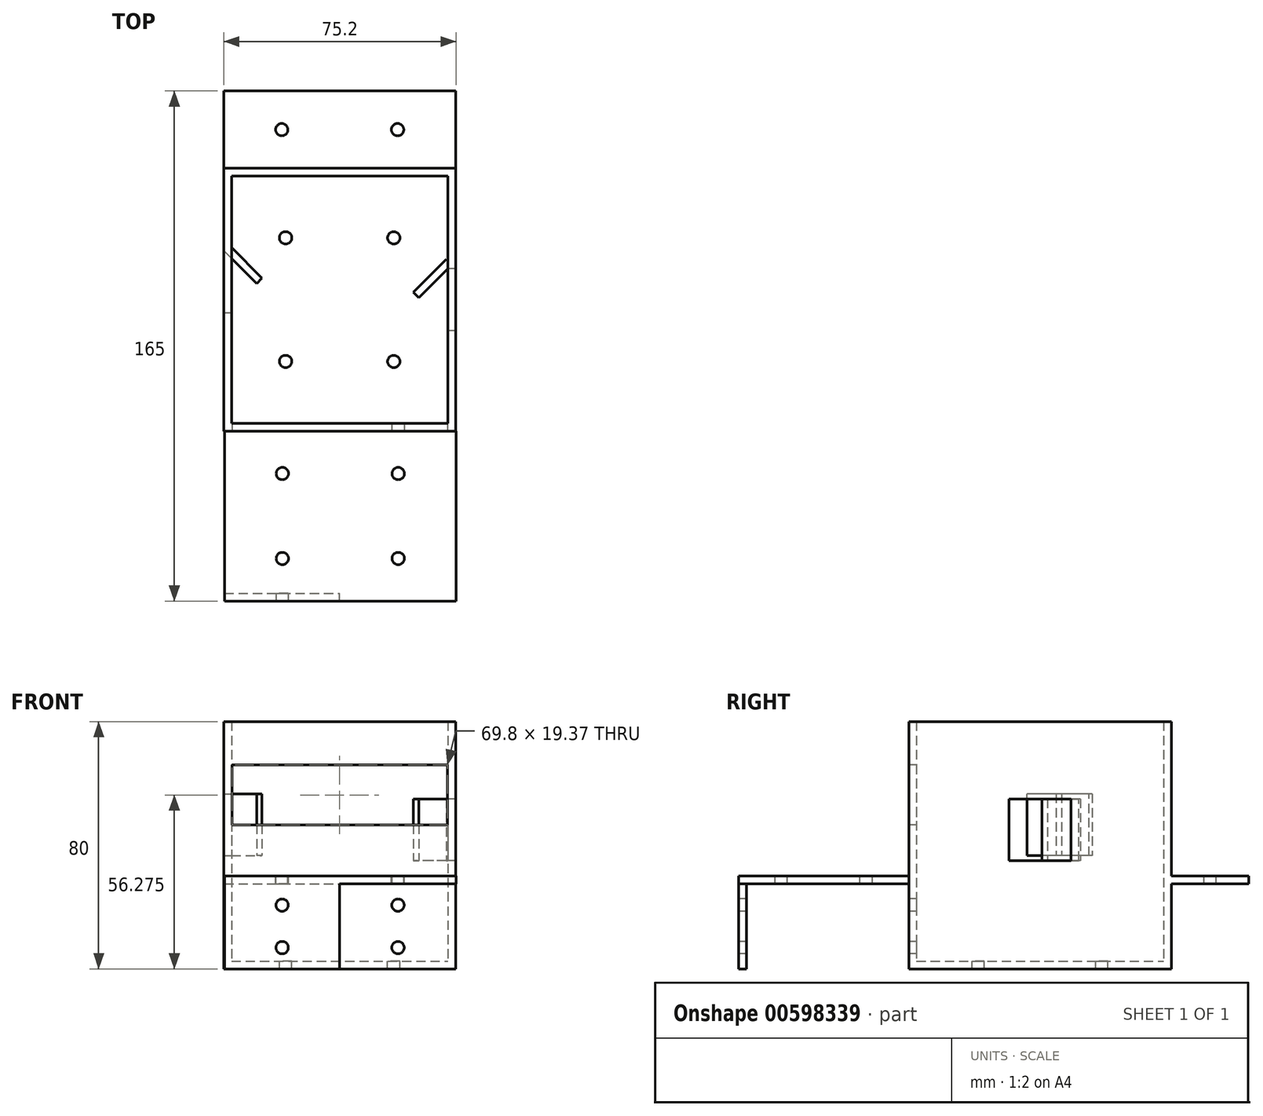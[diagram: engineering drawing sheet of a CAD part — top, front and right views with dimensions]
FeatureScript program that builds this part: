
annotation { "Feature Type Name" : "Feature", "Feature Type Description" : "" }
export const myFeature = defineFeature(function(context is Context, id is Id, definition is map)
    precondition{}
    {
        {
            var Q0;
            Q0=qCreatedBy(makeId("Top.planeOp"),FACE);
            var sketch = newSketch(context, id + "F0", { "sketchPlane" : qUnion([Q0])});
            skPoint(sketch, "E0", {"position": v(-37.5, -42.5) * mm});
            skPoint(sketch, "E1", {"position": v(37.5, 42.5) * mm});
            skLineSegment(sketch, "E2.bottom", {"start": v(-37.5, -42.5) * mm, "end": v(37.5, -42.5) * mm});
            skLineSegment(sketch, "E2.top", {"start": v(-37.5, 42.5) * mm, "end": v(37.5, 42.5) * mm});
            skLineSegment(sketch, "E2.left", {"start": v(-37.5, -42.5) * mm, "end": v(-37.5, 42.5) * mm});
            skLineSegment(sketch, "E2.right", {"start": v(37.5, -42.5) * mm, "end": v(37.5, 42.5) * mm});
            skSolve(sketch);
        }
        {
            var Q0;
            Q0=makeQuery(id+"F0.imprint","IMPRINT",FACE,{"disambiguationData":[TD([[makeQuery(id+"F0.imprint","IMPRINT",EDGE,{"derivedFrom":sQuery(id+"F0.wireOp",EDGE,"E2.bottom")}),1.0]])]});
            extrude(context, id + "F1", {"entities" : qUnion([Q0]), "depth" : 80 * mm, "offsetDistance" : 25.4 * mm});
        }
        {
            var Q0;
            Q0=makeQuery(id+"F1.opExtrude","CAP_FACE",FACE,{"disambiguationData":[OSD([sQuery(id+"F0.wireOp",EDGE,"E2.bottom"),sQuery(id+"F0.wireOp",EDGE,"E2.top"),sQuery(id+"F0.wireOp",EDGE,"E2.left"),sQuery(id+"F0.wireOp",EDGE,"E2.right")])],"isStart":false});
            shell(context, id + "F2", {"entities" : qUnion([Q0]), "thickness" : 2.5 * mm});
        }
        {
            var Q0;
            Q0=makeQuery(id+"F1.opExtrude","SWEPT_FACE",FACE,{"disambiguationData":[OSD([sQuery(id+"F0.wireOp",EDGE,"E2.bottom")])]});
            var sketch = newSketch(context, id + "F3", { "sketchPlane" : qUnion([Q0])});
            skPoint(sketch, "E3", {"position": v(-37.5, 65.96) * mm});
            skPoint(sketch, "E4", {"position": v(37.5, 66.59) * mm});
            skLineSegment(sketch, "E5", {"start": v(-37.5, 65.96) * mm, "end": v(-37.5, 45.96) * mm});
            skLineSegment(sketch, "E6", {"start": v(37.5, 66.59) * mm, "end": v(37.5, 46.59) * mm});
            skPoint(sketch, "E7", {"position": v(-37.5, 45.96) * mm});
            skLineSegment(sketch, "E8", {"start": v(-37.5, 65.96) * mm, "end": v(-34.9, 65.96) * mm});
            skLineSegment(sketch, "E9", {"start": v(37.5, 46.59) * mm, "end": v(34.9, 46.59) * mm});
            skLineSegment(sketch, "E10.bottom", {"start": v(-34.9, 65.96) * mm, "end": v(34.9, 65.96) * mm});
            skLineSegment(sketch, "E10.top", {"start": v(-34.9, 46.59) * mm, "end": v(34.9, 46.59) * mm});
            skLineSegment(sketch, "E10.left", {"start": v(-34.9, 65.96) * mm, "end": v(-34.9, 46.59) * mm});
            skLineSegment(sketch, "E10.right", {"start": v(34.9, 65.96) * mm, "end": v(34.9, 46.59) * mm});
            skSolve(sketch);
        }
        {
            var Q0;
            Q0=makeQuery(id+"F3.imprint","IMPRINT",FACE,{"disambiguationData":[TD([[makeQuery(id+"F3.imprint","IMPRINT",EDGE,{"derivedFrom":sQuery(id+"F3.wireOp",EDGE,"E10.bottom")}),-1.0]])]});
            extrude(context, id + "F4", {"entities" : qUnion([Q0]), "operationType" : NewBodyOperationType.REMOVE, "oppositeDirection" : true, "depth" : 2.5 * mm, "offsetDistance" : 25.4 * mm});
        }
        {
            var Q0;
            Q0=qCreatedBy(makeId("Right.planeOp"),FACE);
            var sketch = newSketch(context, id + "F5", { "sketchPlane" : qUnion([Q0])});
            skPoint(sketch, "E11", {"position": v(5.82, 46.62) * mm});
            skLineSegment(sketch, "E12.bottom", {"start": v(-4.18, 56.62) * mm, "end": v(15.82, 56.62) * mm});
            skLineSegment(sketch, "E12.top", {"start": v(-4.18, 36.62) * mm, "end": v(15.82, 36.62) * mm});
            skLineSegment(sketch, "E12.left", {"start": v(-4.18, 56.62) * mm, "end": v(-4.18, 36.62) * mm});
            skLineSegment(sketch, "E12.right", {"start": v(15.82, 56.62) * mm, "end": v(15.82, 36.62) * mm});
            skSolve(sketch);
        }
        {
            var Q0;
            Q0 = qSketchRegion(id + "F5", true);
            extrude(context, id + "F6", {"entities" : qUnion([Q0]), "operationType" : NewBodyOperationType.REMOVE, "oppositeDirection" : true, "depth" : 85 * mm, "offsetDistance" : 25.4 * mm});
        }
        {
            var Q0;
            Q0=qCreatedBy(makeId("Right.planeOp"),FACE);
            var sketch = newSketch(context, id + "F7", { "sketchPlane" : qUnion([Q0])});
            skLineSegment(sketch, "E13.bottom", {"start": v(10, 55) * mm, "end": v(-10, 55) * mm});
            skLineSegment(sketch, "E13.top", {"start": v(10, 35) * mm, "end": v(-10, 35) * mm});
            skLineSegment(sketch, "E13.left", {"start": v(10, 55) * mm, "end": v(10, 35) * mm});
            skLineSegment(sketch, "E13.right", {"start": v(-10, 55) * mm, "end": v(-10, 35) * mm});
            skPoint(sketch, "E13.middle", {"position": v(0, 45) * mm});
            skSolve(sketch);
        }
        {
            var Q0;
            Q0 = qSketchRegion(id + "F7", true);
            extrude(context, id + "F8", {"entities" : qUnion([Q0]), "operationType" : NewBodyOperationType.REMOVE, "depth" : 40 * mm, "offsetDistance" : 25.4 * mm});
        }
        {
            var Q0;
            Q0=makeQuery(id+"F8.boolean.opBoolean","INTERSECT",EDGE,{"derivedFrom":[makeQuery(id+"F2.opShell","OFFSET_FACE",FACE,{"disambiguationData":[OSD([sQuery(id+"F0.wireOp",EDGE,"E2.right")])]}),makeQuery(id+"F8.opExtrude","SWEPT_FACE",FACE,{"disambiguationData":[OSD([sQuery(id+"F7.wireOp",EDGE,"E13.left")])]})]});
            cPlane(context, id + "F9", {"entities" : qUnion([Q0]), "cplaneType" : CPlaneType.LINE_ANGLE, "offset" : 25.4 * mm, "angle" : 45 * degree, "width" : 152.4 * mm, "height" : 152.4 * mm});
        }
        {
            var Q0;
            Q0=makeQuery(id+"F1.opExtrude","SWEPT_FACE",FACE,{"disambiguationData":[OSD([sQuery(id+"F0.wireOp",EDGE,"E2.bottom")])]});
            var sketch = newSketch(context, id + "F10", { "sketchPlane" : qUnion([Q0])});
            skLineSegment(sketch, "E14", {"start": v(0, 0) * mm, "end": v(0, 27.5) * mm});
            skPoint(sketch, "E14.endSnap0", {"position": v(0, 0) * mm});
            skLineSegment(sketch, "E15", {"start": v(0, 27.5) * mm, "end": v(37.5, 27.5) * mm});
            skLineSegment(sketch, "E16", {"start": v(37.5, 27.5) * mm, "end": v(-37.5, 27.5) * mm});
            skSolve(sketch);
        }
        {
            var Q0;
            Q0=sQuery(id+"F10.wireOp",EDGE,"E16");
            cPlane(context, id + "F11", {"entities" : qUnion([Q0]), "cplaneType" : CPlaneType.LINE_ANGLE, "offset" : 25.4 * mm, "angle" : 90 * degree, "width" : 152.4 * mm, "height" : 152.4 * mm});
        }
        {
            var Q0;
            Q0=qCreatedBy(id+"F11.planeOp",FACE);
            var sketch = newSketch(context, id + "F12", { "sketchPlane" : qUnion([Q0])});
            skLineSegment(sketch, "E17", {"start": v(0.2, 0) * mm, "end": v(0.2, -42.5) * mm});
            skLineSegment(sketch, "E18", {"start": v(0.2, -42.5) * mm, "end": v(37.7, -42.5) * mm});
            skLineSegment(sketch, "E19", {"start": v(37.7, -42.5) * mm, "end": v(37.7, -95) * mm});
            skLineSegment(sketch, "E20", {"start": v(0.2, -42.5) * mm, "end": v(-37.3, -42.5) * mm});
            skLineSegment(sketch, "E21.bottom", {"start": v(-37.3, -42.5) * mm, "end": v(37.7, -42.5) * mm});
            skLineSegment(sketch, "E21.top", {"start": v(-37.3, -95) * mm, "end": v(37.7, -95) * mm});
            skLineSegment(sketch, "E21.left", {"start": v(-37.3, -42.5) * mm, "end": v(-37.3, -95) * mm});
            skSolve(sketch);
        }
        {
            var Q0;
            Q0=makeQuery(id+"F12.imprint","IMPRINT",FACE,{"disambiguationData":[TD([[makeQuery(id+"F12.imprint","IMPRINT",EDGE,{"derivedFrom":sQuery(id+"F12.wireOp",EDGE,"E21.top")}),1.0]])]});
            extrude(context, id + "F13", {"entities" : qUnion([Q0]), "operationType" : NewBodyOperationType.ADD, "depth" : 2.5 * mm, "offsetDistance" : 25.4 * mm});
        }
        {
            var Q0;
            Q0=makeQuery(id+"F13.opExtrude","SWEPT_FACE",FACE,{"disambiguationData":[OSD([sQuery(id+"F12.wireOp",EDGE,"E21.top")])]});
            var sketch = newSketch(context, id + "F14", { "sketchPlane" : qUnion([Q0])});
            skLineSegment(sketch, "E22", {"start": v(0.2, 27.5) * mm, "end": v(0, -7.5) * mm});
            skLineSegment(sketch, "E23.bottom", {"start": v(0, 0) * mm, "end": v(37.7, 0) * mm});
            skLineSegment(sketch, "E23.top", {"start": v(0, 27.5) * mm, "end": v(37.7, 27.5) * mm});
            skLineSegment(sketch, "E23.left", {"start": v(0, 0) * mm, "end": v(0, 27.5) * mm});
            skLineSegment(sketch, "E23.right", {"start": v(37.7, 0) * mm, "end": v(37.7, 27.5) * mm});
            skLineSegment(sketch, "E24.bottom", {"start": v(0, 0) * mm, "end": v(-37.3, 0) * mm});
            skLineSegment(sketch, "E24.top", {"start": v(0, 27.5) * mm, "end": v(-37.3, 27.5) * mm});
            skLineSegment(sketch, "E24.right", {"start": v(-37.3, 0) * mm, "end": v(-37.3, 27.5) * mm});
            skPoint(sketch, "E25", {"position": v(37.7, 0) * mm});
            skPoint(sketch, "E26", {"position": v(-37.3, 27.5) * mm});
            skLineSegment(sketch, "E27.bottom", {"start": v(-37.3, 27.5) * mm, "end": v(37.7, 27.5) * mm});
            skLineSegment(sketch, "E27.top", {"start": v(-37.3, 0) * mm, "end": v(37.7, 0) * mm});
            skLineSegment(sketch, "E27.left", {"start": v(-37.3, 27.5) * mm, "end": v(-37.3, 0) * mm});
            skLineSegment(sketch, "E27.right", {"start": v(37.7, 27.5) * mm, "end": v(37.7, 0) * mm});
            skSolve(sketch);
        }
        {
            var Q0;
            Q0=qCreatedBy(id+"F9.planeOp",FACE);
            var sketch = newSketch(context, id + "F15", { "sketchPlane" : qUnion([Q0])});
            skLineSegment(sketch, "E28.0", {"start": v(-33.59, 55) * mm, "end": v(-33.59, 35) * mm});
            skLineSegment(sketch, "E29.bottom", {"start": v(-33.59, 55) * mm, "end": v(-18.59, 55) * mm});
            skLineSegment(sketch, "E29.top", {"start": v(-33.59, 35) * mm, "end": v(-18.59, 35) * mm});
            skLineSegment(sketch, "E29.right", {"start": v(-18.59, 55) * mm, "end": v(-18.59, 35) * mm});
            skPoint(sketch, "E30.0", {"position": v(28.28, 2.5) * mm});
            skSolve(sketch);
        }
        {
            var Q0;
            Q0=makeQuery(id+"F15.imprint","IMPRINT",FACE,{"disambiguationData":[TD([[makeQuery(id+"F15.imprint","IMPRINT",EDGE,{"derivedFrom":sQuery(id+"F15.wireOp",EDGE,"E29.bottom")}),-1.0]])]});
            extrude(context, id + "F16", {"entities" : qUnion([Q0]), "operationType" : NewBodyOperationType.ADD, "depth" : 2.5 * mm, "offsetDistance" : 25 * mm});
        }
        {
            var Q0;
            Q0=makeQuery(id+"F6.boolean.opBoolean","INTERSECT",EDGE,{"derivedFrom":[makeQuery(id+"F1.opExtrude","SWEPT_FACE",FACE,{"disambiguationData":[OSD([sQuery(id+"F0.wireOp",EDGE,"E2.left")])]}),makeQuery(id+"F6.opExtrude","SWEPT_FACE",FACE,{"disambiguationData":[OSD([sQuery(id+"F5.wireOp",EDGE,"E12.right")])]})]});
            cPlane(context, id + "F17", {"entities" : qUnion([Q0]), "cplaneType" : CPlaneType.LINE_ANGLE, "offset" : 25 * mm, "angle" : 45 * degree, "width" : 150 * mm, "height" : 150 * mm});
        }
        {
            var Q0;
            Q0=qCreatedBy(id+"F17.planeOp",FACE);
            var sketch = newSketch(context, id + "F18", { "sketchPlane" : qUnion([Q0])});
            skLineSegment(sketch, "E31.0", {"start": v(37.7, 36.62) * mm, "end": v(37.7, 56.62) * mm});
            skLineSegment(sketch, "E32.bottom", {"start": v(37.7, 56.62) * mm, "end": v(37.7, 56.62) * mm});
            skLineSegment(sketch, "E32.top", {"start": v(37.7, 36.62) * mm, "end": v(37.7, 36.62) * mm});
            skLineSegment(sketch, "E32.left", {"start": v(37.7, 56.62) * mm, "end": v(37.7, 36.62) * mm});
            skLineSegment(sketch, "E32.right", {"start": v(37.7, 56.62) * mm, "end": v(37.7, 36.62) * mm});
            skLineSegment(sketch, "E33.bottom", {"start": v(37.7, 56.62) * mm, "end": v(22.7, 56.62) * mm});
            skLineSegment(sketch, "E33.top", {"start": v(37.7, 36.62) * mm, "end": v(22.7, 36.62) * mm});
            skLineSegment(sketch, "E33.right", {"start": v(22.7, 56.62) * mm, "end": v(22.7, 36.62) * mm});
            skSolve(sketch);
        }
        {
            var Q0;
            Q0=makeQuery(id+"F18.imprint","IMPRINT",FACE,{"disambiguationData":[TD([[makeQuery(id+"F18.imprint","IMPRINT",EDGE,{"derivedFrom":sQuery(id+"F18.wireOp",EDGE,"E33.bottom")}),1.0]])]});
            extrude(context, id + "F19", {"entities" : qUnion([Q0]), "operationType" : NewBodyOperationType.ADD, "depth" : 2.5 * mm, "offsetDistance" : 25 * mm});
        }
        {
            var Q0;
            {var subQ0=sQuery(id+"F14.wireOp",EDGE,"E23.left");Q0=makeQuery(id+"F14.imprint","IMPRINT",FACE,{"disambiguationData":[TD([[makeQuery(id+"F14.imprint","IMPRINT",EDGE,{"derivedFrom":subQ0}),1.0]])]});}
            var Q1;
            {var subQ5=sQuery(id+"F14.wireOp",EDGE,"E27.right");Q1=makeQuery(id+"F14.imprint","IMPRINT",FACE,{"disambiguationData":[TD([[makeQuery(id+"F14.imprint","IMPRINT",EDGE,{"derivedFrom":subQ5}),-1.0]])]});}
            var Q2;
            {var subQ0=sQuery(id+"F12.wireOp",EDGE,"E21.top");Q2=makeQuery(id+"F14.imprint","IMPRINT",FACE,{"disambiguationData":[TD([[makeQuery(id+"F14.imprint","IMPRINT",EDGE,{"derivedFrom":makeQuery(id+"F13.opExtrude","CAP_EDGE",EDGE,{"disambiguationData":[OSD([subQ0])],"isStart":false})}),-1.0]])]});}
            extrude(context, id + "F20", {"entities" : qUnion([Q0, Q1, Q2]), "operationType" : NewBodyOperationType.ADD, "depth" : 2.5 * mm, "offsetDistance" : 25 * mm});
        }
        {
            var Q0;
            Q0=qCreatedBy(id+"F11.planeOp",FACE);
            var sketch = newSketch(context, id + "F21", { "sketchPlane" : qUnion([Q0])});
            skLineSegment(sketch, "E34", {"start": v(0, 0) * mm, "end": v(0, 42.5) * mm});
            skPoint(sketch, "E35", {"position": v(0, 42.5) * mm});
            skLineSegment(sketch, "E36", {"start": v(0, 42.5) * mm, "end": v(-37.5, 42.5) * mm});
            skLineSegment(sketch, "E37", {"start": v(-37.5, 42.5) * mm, "end": v(-37.5, 67.5) * mm});
            skLineSegment(sketch, "E38", {"start": v(0, 42.5) * mm, "end": v(37.5, 42.5) * mm});
            skLineSegment(sketch, "E39.bottom", {"start": v(37.5, 42.5) * mm, "end": v(-37.5, 42.5) * mm});
            skLineSegment(sketch, "E39.top", {"start": v(37.5, 67.5) * mm, "end": v(-37.5, 67.5) * mm});
            skLineSegment(sketch, "E39.left", {"start": v(37.5, 42.5) * mm, "end": v(37.5, 67.5) * mm});
            skLineSegment(sketch, "E40", {"start": v(0, 42.5) * mm, "end": v(0, 55) * mm});
            skLineSegment(sketch, "E41", {"start": v(0, 55) * mm, "end": v(18.75, 55) * mm});
            skLineSegment(sketch, "E42", {"start": v(0, 55) * mm, "end": v(-18.75, 55) * mm});
            skPoint(sketch, "E43", {"position": v(-18.75, 55) * mm});
            skPoint(sketch, "E44", {"position": v(18.75, 55) * mm});
            skSolve(sketch);
        }
        {
            var Q0;
            Q0=makeQuery(id+"F21.imprint","IMPRINT",FACE,{"disambiguationData":[TD([[makeQuery(id+"F21.imprint","IMPRINT",EDGE,{"derivedFrom":sQuery(id+"F21.wireOp",EDGE,"E39.top")}),1.0]])]});
            extrude(context, id + "F22", {"entities" : qUnion([Q0]), "operationType" : NewBodyOperationType.ADD, "depth" : 2.5 * mm, "offsetDistance" : 25 * mm});
        }
        {
            var Q0;
            Q0=makeQuery(id+"F22.opExtrude","CAP_FACE",FACE,{"disambiguationData":[OSD([sQuery(id+"F21.wireOp",EDGE,"E39.bottom"),sQuery(id+"F21.wireOp",EDGE,"E39.top"),sQuery(id+"F21.wireOp",EDGE,"E39.left"),sQuery(id+"F21.wireOp",EDGE,"E37")])],"isStart":false});
            var sketch = newSketch(context, id + "F23", { "sketchPlane" : qUnion([Q0])});
            skPoint(sketch, "E45.endSnap0", {"position": v(0, 42.5) * mm});
            skPoint(sketch, "E46", {"position": v(-18.75, 55) * mm});
            skPoint(sketch, "E47", {"position": v(18.75, 55) * mm});
            skCircle(sketch, "E48", {"center": v(-18.75, 55) * mm, "radius": 2 * mm});
            skCircle(sketch, "E49", {"center": v(18.75, 55) * mm, "radius": 2 * mm});
            skSolve(sketch);
        }
        {
            var Q0;
            Q0=sQuery(id+"F23.wireOp",VERTEX,"E46");
            var Q1;
            Q1=sQuery(id+"F23.wireOp",VERTEX,"E47");
            var Q2;
            Q2=makeQuery(id+"F1.opExtrude","SWEPT_BODY",BODY,{"disambiguationData":[OSD([sQuery(id+"F0.wireOp",EDGE,"E2.bottom"),sQuery(id+"F0.wireOp",EDGE,"E2.top"),sQuery(id+"F0.wireOp",EDGE,"E2.left"),sQuery(id+"F0.wireOp",EDGE,"E2.right")])]});
            hole(context, id + "F24", {"style" : HoleStyle.SIMPLE, "endStyle" : HoleEndStyle.THROUGH, "holeDiameter" : 4 * mm, "majorDiameter" : 5 * mm, "isTappedThrough" : true, "tappedDepth" : 12 * mm, "tapClearance" : 3, "locations" : qUnion([Q0, Q1]), "scope" : qUnion([Q2])});
        }
        {
            var Q0;
            Q0=makeQuery(id+"F20.opExtrude","CAP_FACE",FACE,{"disambiguationData":[OSD([sQuery(id+"F12.wireOp",EDGE,"E21.top"),sQuery(id+"F12.wireOp",EDGE,"E21.left"),sQuery(id+"F12.wireOp",EDGE,"E19"),sQuery(id+"F14.wireOp",EDGE,"E22"),sQuery(id+"F14.wireOp",EDGE,"E23.left"),sQuery(id+"F14.wireOp",EDGE,"E27.bottom"),sQuery(id+"F14.wireOp",EDGE,"E27.top"),sQuery(id+"F14.wireOp",EDGE,"E27.left"),sQuery(id+"F14.wireOp",EDGE,"E27.right")])],"isStart":false});
            var sketch = newSketch(context, id + "F25", { "sketchPlane" : qUnion([Q0])});
            skPoint(sketch, "E50", {"position": v(-18.63, 20.62) * mm});
            skPoint(sketch, "E51", {"position": v(-18.63, 6.87) * mm});
            skPoint(sketch, "E52", {"position": v(18.87, 6.87) * mm});
            skPoint(sketch, "E53", {"position": v(18.87, 20.62) * mm});
            skSolve(sketch);
        }
        {
            var Q0;
            Q0=sQuery(id+"F25.wireOp",VERTEX,"E50");
            var Q1;
            Q1=sQuery(id+"F25.wireOp",VERTEX,"E51");
            var Q2;
            Q2=sQuery(id+"F25.wireOp",VERTEX,"E52");
            var Q3;
            Q3=sQuery(id+"F25.wireOp",VERTEX,"E53");
            var Q4;
            Q4=makeQuery(id+"F1.opExtrude","SWEPT_BODY",BODY,{"disambiguationData":[OSD([sQuery(id+"F0.wireOp",EDGE,"E2.bottom"),sQuery(id+"F0.wireOp",EDGE,"E2.top"),sQuery(id+"F0.wireOp",EDGE,"E2.left"),sQuery(id+"F0.wireOp",EDGE,"E2.right")])]});
            hole(context, id + "F26", {"style" : HoleStyle.SIMPLE, "endStyle" : HoleEndStyle.BLIND, "holeDiameter" : 4 * mm, "majorDiameter" : 5 * mm, "holeDepth" : 12 * mm, "isTappedThrough" : true, "tappedDepth" : 12 * mm, "tapClearance" : 3, "locations" : qUnion([Q0, Q1, Q2, Q3]), "scope" : qUnion([Q4])});
        }
        {
            var Q0;
            {var subQ0=sQuery(id+"F12.wireOp",EDGE,"E21.top");Q0=makeQuery(id+"F20.boolean.opBoolean","MERGE",FACE,{"derivedFrom":[makeQuery(id+"F13.opExtrude","CAP_FACE",FACE,{"disambiguationData":[OSD([sQuery(id+"F12.wireOp",EDGE,"E21.bottom"),subQ0,sQuery(id+"F12.wireOp",EDGE,"E21.left"),sQuery(id+"F12.wireOp",EDGE,"E19")])],"isStart":false}),makeQuery(id+"F20.opExtrude","SWEPT_FACE",FACE,{"disambiguationData":[OSD([subQ0])]})]});}
            var sketch = newSketch(context, id + "F27", { "sketchPlane" : qUnion([Q0])});
            skPoint(sketch, "E54", {"position": v(-18.55, -56.25) * mm});
            skPoint(sketch, "E55", {"position": v(18.95, -56.25) * mm});
            skPoint(sketch, "E56", {"position": v(18.95, -83.75) * mm});
            skPoint(sketch, "E57", {"position": v(-18.55, -83.75) * mm});
            skSolve(sketch);
        }
        {
            var Q0;
            Q0=sQuery(id+"F27.wireOp",VERTEX,"E54");
            var Q1;
            Q1=sQuery(id+"F27.wireOp",VERTEX,"E55");
            var Q2;
            Q2=sQuery(id+"F27.wireOp",VERTEX,"E56");
            var Q3;
            Q3=sQuery(id+"F27.wireOp",VERTEX,"E57");
            var Q4;
            Q4=makeQuery(id+"F1.opExtrude","SWEPT_BODY",BODY,{"disambiguationData":[OSD([sQuery(id+"F0.wireOp",EDGE,"E2.bottom"),sQuery(id+"F0.wireOp",EDGE,"E2.top"),sQuery(id+"F0.wireOp",EDGE,"E2.left"),sQuery(id+"F0.wireOp",EDGE,"E2.right")])]});
            hole(context, id + "F28", {"style" : HoleStyle.SIMPLE, "endStyle" : HoleEndStyle.BLIND, "holeDiameter" : 4 * mm, "majorDiameter" : 5 * mm, "holeDepth" : 12 * mm, "isTappedThrough" : true, "tappedDepth" : 12 * mm, "tapClearance" : 3, "locations" : qUnion([Q0, Q1, Q2, Q3]), "scope" : qUnion([Q4])});
        }
        {
            var Q0;
            Q0=makeQuery(id+"F2.opShell","OFFSET_FACE",FACE,{"disambiguationData":[OSD([sQuery(id+"F0.wireOp",EDGE,"E2.bottom"),sQuery(id+"F0.wireOp",EDGE,"E2.top"),sQuery(id+"F0.wireOp",EDGE,"E2.left"),sQuery(id+"F0.wireOp",EDGE,"E2.right")])]});
            var sketch = newSketch(context, id + "F29", { "sketchPlane" : qUnion([Q0])});
            skPoint(sketch, "E58", {"position": v(-17.5, 20) * mm});
            skPoint(sketch, "E59", {"position": v(17.5, 20) * mm});
            skPoint(sketch, "E60", {"position": v(-17.5, -20) * mm});
            skPoint(sketch, "E61", {"position": v(17.5, -20) * mm});
            skSolve(sketch);
        }
        {
            var Q0;
            Q0=sQuery(id+"F29.wireOp",VERTEX,"E58");
            var Q1;
            Q1=sQuery(id+"F29.wireOp",VERTEX,"E59");
            var Q2;
            Q2=sQuery(id+"F29.wireOp",VERTEX,"E60");
            var Q3;
            Q3=sQuery(id+"F29.wireOp",VERTEX,"E61");
            var Q4;
            Q4=makeQuery(id+"F1.opExtrude","SWEPT_BODY",BODY,{"disambiguationData":[OSD([sQuery(id+"F0.wireOp",EDGE,"E2.bottom"),sQuery(id+"F0.wireOp",EDGE,"E2.top"),sQuery(id+"F0.wireOp",EDGE,"E2.left"),sQuery(id+"F0.wireOp",EDGE,"E2.right")])]});
            hole(context, id + "F30", {"style" : HoleStyle.SIMPLE, "endStyle" : HoleEndStyle.BLIND, "holeDiameter" : 4 * mm, "majorDiameter" : 5 * mm, "holeDepth" : 12 * mm, "isTappedThrough" : true, "tappedDepth" : 12 * mm, "tapClearance" : 3, "locations" : qUnion([Q0, Q1, Q2, Q3]), "scope" : qUnion([Q4])});
        }
    });
